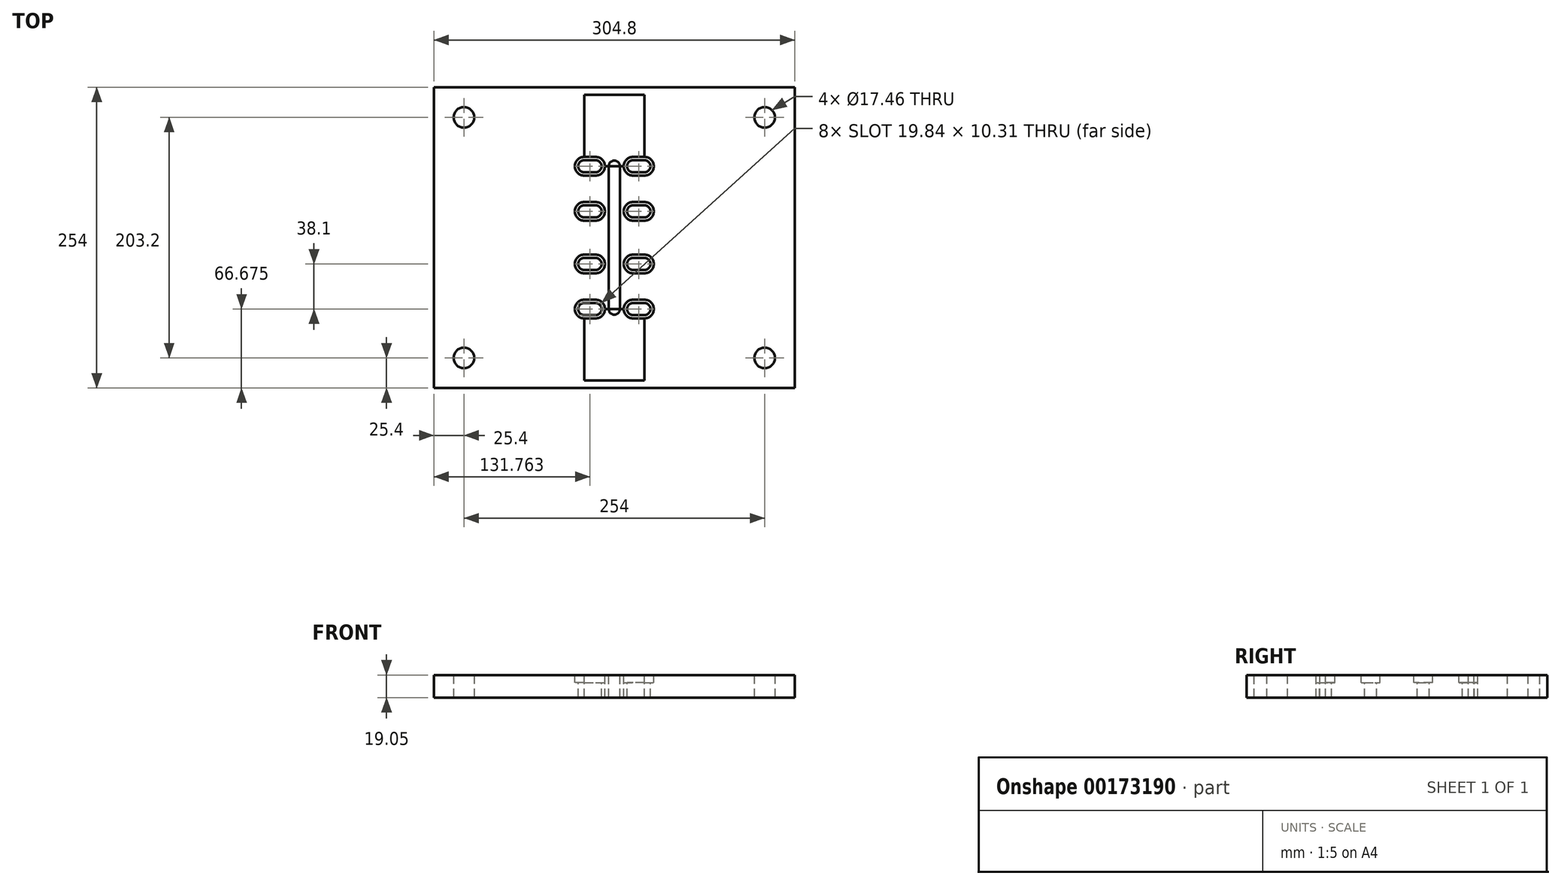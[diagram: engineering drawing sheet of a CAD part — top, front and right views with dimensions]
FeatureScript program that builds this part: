
annotation { "Feature Type Name" : "Feature", "Feature Type Description" : "" }
export const myFeature = defineFeature(function(context is Context, id is Id, definition is map)
    precondition{}
    {
        {
            var Q0;
            Q0=qCreatedBy(makeId("Top.planeOp"),FACE);
            var sketch = newSketch(context, id + "F0", { "sketchPlane" : qUnion([Q0])});
            skLineSegment(sketch, "E0.bottom", {"start": v(-152.4, 127) * mm, "end": v(152.4, 127) * mm});
            skLineSegment(sketch, "E0.top", {"start": v(-152.4, -127) * mm, "end": v(152.4, -127) * mm});
            skLineSegment(sketch, "E0.left", {"start": v(-152.4, 127) * mm, "end": v(-152.4, -127) * mm});
            skLineSegment(sketch, "E0.right", {"start": v(152.4, 127) * mm, "end": v(152.4, -127) * mm});
            skPoint(sketch, "E0.middle", {"position": v(0, 0) * mm});
            skLineSegment(sketch, "E1", {"start": v(0, 127) * mm, "end": v(0, -127) * mm});
            skLineSegment(sketch, "E2", {"start": v(152.4, 0) * mm, "end": v(-152.4, 0) * mm});
            skLineSegment(sketch, "E3.0", {"start": v(-22.22, 101.6) * mm, "end": v(-22.23, -101.6) * mm});
            skLineSegment(sketch, "E4.0", {"start": v(22.23, 101.6) * mm, "end": v(22.22, -101.6) * mm});
            skLineSegment(sketch, "E5.0", {"start": v(101.6, -22.22) * mm, "end": v(-101.6, -22.23) * mm});
            skLineSegment(sketch, "E6.0", {"start": v(101.6, 22.23) * mm, "end": v(-101.6, 22.22) * mm});
            skLineSegment(sketch, "E7.0", {"start": v(101.6, 60.33) * mm, "end": v(-101.6, 60.32) * mm});
            skLineSegment(sketch, "E8.0", {"start": v(101.6, -60.32) * mm, "end": v(-101.6, -60.33) * mm});
            skPoint(sketch, "E9", {"position": v(-22.22, 60.33) * mm});
            skPoint(sketch, "E10", {"position": v(22.23, 60.33) * mm});
            skPoint(sketch, "E11", {"position": v(22.23, 22.23) * mm});
            skPoint(sketch, "E12", {"position": v(-22.22, 22.23) * mm});
            skPoint(sketch, "E13", {"position": v(-22.23, -22.23) * mm});
            skPoint(sketch, "E14", {"position": v(22.22, -60.33) * mm});
            skPoint(sketch, "E15", {"position": v(22.22, -22.22) * mm});
            skPoint(sketch, "E16", {"position": v(-22.23, -60.33) * mm});
            skSolve(sketch);
        }
        {
            var Q0;
            Q0 = qSketchRegion(id + "F0", true);
            var Q1;
            {var subQ0=sQuery(id+"F0.wireOp",EDGE,"E7.0");var subQ1=sQuery(id+"F0.wireOp",EDGE,"E1");var subQ2=makeQuery(id+"F0.imprint","INTERSECT",VERTEX,{"derivedFrom":[subQ1,subQ0]});Q1=makeQuery(id+"F0.imprint","IMPRINT",FACE,{"disambiguationData":[TD([[makeQuery(id+"F0.imprint","IMPRINT",EDGE,{"disambiguationData":[TD([[subQ2,-1.0]])],"derivedFrom":subQ1}),-1.0]])]});}
            var Q2;
            {var subQ0=sQuery(id+"F0.wireOp",EDGE,"E7.0");var subQ1=sQuery(id+"F0.wireOp",EDGE,"E1");var subQ2=makeQuery(id+"F0.imprint","INTERSECT",VERTEX,{"derivedFrom":[subQ1,subQ0]});Q2=makeQuery(id+"F0.imprint","IMPRINT",FACE,{"disambiguationData":[TD([[makeQuery(id+"F0.imprint","IMPRINT",EDGE,{"disambiguationData":[TD([[subQ2,-1.0]])],"derivedFrom":subQ1}),1.0]])]});}
            var Q3;
            {var subQ0=sQuery(id+"F0.wireOp",EDGE,"E6.0");var subQ1=sQuery(id+"F0.wireOp",EDGE,"E1");var subQ2=makeQuery(id+"F0.imprint","INTERSECT",VERTEX,{"derivedFrom":[subQ1,subQ0]});Q3=makeQuery(id+"F0.imprint","IMPRINT",FACE,{"disambiguationData":[TD([[makeQuery(id+"F0.imprint","IMPRINT",EDGE,{"disambiguationData":[TD([[subQ2,-1.0]])],"derivedFrom":subQ1}),1.0]])]});}
            var Q4;
            {var subQ0=sQuery(id+"F0.wireOp",EDGE,"E6.0");var subQ1=sQuery(id+"F0.wireOp",EDGE,"E1");var subQ2=makeQuery(id+"F0.imprint","INTERSECT",VERTEX,{"derivedFrom":[subQ1,subQ0]});Q4=makeQuery(id+"F0.imprint","IMPRINT",FACE,{"disambiguationData":[TD([[makeQuery(id+"F0.imprint","IMPRINT",EDGE,{"disambiguationData":[TD([[subQ2,-1.0]])],"derivedFrom":subQ1}),-1.0]])]});}
            var Q5;
            {var subQ0=sQuery(id+"F0.wireOp",EDGE,"E2");var subQ1=sQuery(id+"F0.wireOp",EDGE,"E1");var subQ2=makeQuery(id+"F0.imprint","INTERSECT",VERTEX,{"derivedFrom":[subQ1,subQ0]});Q5=makeQuery(id+"F0.imprint","IMPRINT",FACE,{"disambiguationData":[TD([[makeQuery(id+"F0.imprint","IMPRINT",EDGE,{"disambiguationData":[TD([[subQ2,-1.0]])],"derivedFrom":subQ1}),-1.0]])]});}
            var Q6;
            {var subQ0=sQuery(id+"F0.wireOp",EDGE,"E2");var subQ1=sQuery(id+"F0.wireOp",EDGE,"E1");var subQ2=makeQuery(id+"F0.imprint","INTERSECT",VERTEX,{"derivedFrom":[subQ1,subQ0]});Q6=makeQuery(id+"F0.imprint","IMPRINT",FACE,{"disambiguationData":[TD([[makeQuery(id+"F0.imprint","IMPRINT",EDGE,{"disambiguationData":[TD([[subQ2,-1.0]])],"derivedFrom":subQ1}),1.0]])]});}
            var Q7;
            {var subQ0=sQuery(id+"F0.wireOp",EDGE,"E5.0");var subQ1=sQuery(id+"F0.wireOp",EDGE,"E1");var subQ2=makeQuery(id+"F0.imprint","INTERSECT",VERTEX,{"derivedFrom":[subQ1,subQ0]});Q7=makeQuery(id+"F0.imprint","IMPRINT",FACE,{"disambiguationData":[TD([[makeQuery(id+"F0.imprint","IMPRINT",EDGE,{"disambiguationData":[TD([[subQ2,-1.0]])],"derivedFrom":subQ1}),1.0]])]});}
            var Q8;
            {var subQ0=sQuery(id+"F0.wireOp",EDGE,"E5.0");var subQ1=sQuery(id+"F0.wireOp",EDGE,"E1");var subQ2=makeQuery(id+"F0.imprint","INTERSECT",VERTEX,{"derivedFrom":[subQ1,subQ0]});Q8=makeQuery(id+"F0.imprint","IMPRINT",FACE,{"disambiguationData":[TD([[makeQuery(id+"F0.imprint","IMPRINT",EDGE,{"disambiguationData":[TD([[subQ2,-1.0]])],"derivedFrom":subQ1}),-1.0]])]});}
            extrude(context, id + "F1", {"entities" : qUnion([Q0, Q1, Q2, Q3, Q4, Q5, Q6, Q7, Q8]), "depth" : 19.05 * mm});
        }
        {
            var Q0;
            Q0=makeQuery(id+"F1.opExtrude","CAP_FACE",FACE,{"disambiguationData":[OSD([sQuery(id+"F0.wireOp",EDGE,"E0.bottom"),sQuery(id+"F0.wireOp",EDGE,"E0.top"),sQuery(id+"F0.wireOp",EDGE,"E0.left"),sQuery(id+"F0.wireOp",EDGE,"E0.right")])],"isStart":false});
            var sketch = newSketch(context, id + "F2", { "sketchPlane" : qUnion([Q0])});
            skLineSegment(sketch, "E17", {"start": v(0, 127) * mm, "end": v(0, 120.65) * mm});
            skLineSegment(sketch, "E18", {"start": v(25.4, 127) * mm, "end": v(25.4, -127) * mm});
            skLineSegment(sketch, "E19", {"start": v(-25.4, -127) * mm, "end": v(-25.4, 127) * mm});
            skLineSegment(sketch, "E20", {"start": v(-152.4, 0) * mm, "end": v(152.4, 0) * mm});
            skLineSegment(sketch, "E21", {"start": v(152.4, 22.22) * mm, "end": v(-10.72, 22.22) * mm});
            skLineSegment(sketch, "E22", {"start": v(-152.4, 60.32) * mm, "end": v(152.4, 60.32) * mm});
            skLineSegment(sketch, "E23", {"start": v(152.4, -22.22) * mm, "end": v(-152.4, -22.23) * mm});
            skLineSegment(sketch, "E24", {"start": v(-152.4, -60.33) * mm, "end": v(152.4, -60.32) * mm});
            skLineSegment(sketch, "E25.0", {"start": v(-15.87, -101.6) * mm, "end": v(-15.88, 101.6) * mm});
            skLineSegment(sketch, "E26.0", {"start": v(15.87, 101.6) * mm, "end": v(15.88, -101.6) * mm});
            skLineSegment(sketch, "E27.0", {"start": v(146.05, -120.65) * mm, "end": v(146.05, 120.65) * mm});
            skLineSegment(sketch, "E27.1", {"start": v(-146.05, -120.65) * mm, "end": v(146.05, -120.65) * mm});
            skLineSegment(sketch, "E27.2", {"start": v(-146.05, 120.65) * mm, "end": v(-146.05, -120.65) * mm});
            skLineSegment(sketch, "E27.3", {"start": v(146.05, 120.65) * mm, "end": v(-146.05, 120.65) * mm});
            skArc(sketch, "E28", {"start": v(-25.4, 27.38) * mm, "mid": v(-30.56, 22.22) * mm, "end": v(-25.4, 17.07) * mm});
            skArc(sketch, "E29", {"start": v(-15.88, 17.07) * mm, "mid": v(-10.72, 22.22) * mm, "end": v(-15.88, 27.38) * mm});
            skLineSegment(sketch, "E30", {"start": v(-25.4, 27.38) * mm, "end": v(-15.88, 27.38) * mm});
            skLineSegment(sketch, "E31", {"start": v(-25.4, 17.07) * mm, "end": v(-15.88, 17.07) * mm});
            skLineSegment(sketch, "E32", {"start": v(-152.4, 41.27) * mm, "end": v(152.4, 41.28) * mm});
            skLineSegment(sketch, "E33", {"start": v(-152.4, -41.28) * mm, "end": v(152.4, -41.27) * mm});
            skLineSegment(sketch, "E34.trimOffspring", {"start": v(-146.05, 22.23) * mm, "end": v(-152.4, 22.23) * mm});
            skLineSegment(sketch, "E35.trimOffspring", {"start": v(-15.88, 22.22) * mm, "end": v(-25.4, 22.22) * mm});
            skArc(sketch, "E36.0.startCap", {"start": v(-15.88, 30.16) * mm, "mid": v(-7.94, 22.22) * mm, "end": v(-15.88, 14.29) * mm});
            skArc(sketch, "E36.0.endCap", {"start": v(-25.4, 14.29) * mm, "mid": v(-33.34, 22.22) * mm, "end": v(-25.4, 30.16) * mm});
            skLineSegment(sketch, "E36.0.left", {"start": v(-15.88, 14.29) * mm, "end": v(-25.4, 14.29) * mm});
            skLineSegment(sketch, "E36.0.right", {"start": v(-15.88, 30.16) * mm, "end": v(-25.4, 30.16) * mm});
            skLineSegment(sketch, "E37.MirrorCS", {"start": v(-15.88, 52.39) * mm, "end": v(-25.4, 52.39) * mm});
            skArc(sketch, "E38.MirrorCS", {"start": v(-15.88, 52.39) * mm, "mid": v(-7.94, 60.33) * mm, "end": v(-15.88, 68.26) * mm});
            skLineSegment(sketch, "E39.MirrorCS", {"start": v(-15.88, 68.26) * mm, "end": v(-25.4, 68.26) * mm});
            skArc(sketch, "E40.MirrorCS", {"start": v(-25.4, 68.26) * mm, "mid": v(-33.34, 60.32) * mm, "end": v(-25.4, 52.39) * mm});
            skArc(sketch, "E41.MirrorCS", {"start": v(-25.4, 55.17) * mm, "mid": v(-30.56, 60.32) * mm, "end": v(-25.4, 65.48) * mm});
            skLineSegment(sketch, "E42.MirrorCS", {"start": v(-25.4, 55.17) * mm, "end": v(-15.88, 55.17) * mm});
            skArc(sketch, "E43.MirrorCS", {"start": v(-15.88, 65.48) * mm, "mid": v(-10.72, 60.33) * mm, "end": v(-15.88, 55.17) * mm});
            skLineSegment(sketch, "E44.MirrorCS", {"start": v(-25.4, 65.48) * mm, "end": v(-15.88, 65.48) * mm});
            skLineSegment(sketch, "E45.MirrorCS", {"start": v(15.88, 68.26) * mm, "end": v(25.4, 68.26) * mm});
            skArc(sketch, "E46.MirrorCS", {"start": v(15.88, 52.39) * mm, "mid": v(7.94, 60.33) * mm, "end": v(15.88, 68.26) * mm});
            skLineSegment(sketch, "E47.MirrorCS", {"start": v(15.88, 52.39) * mm, "end": v(25.4, 52.39) * mm});
            skArc(sketch, "E48.MirrorCS", {"start": v(25.4, 68.26) * mm, "mid": v(33.34, 60.32) * mm, "end": v(25.4, 52.39) * mm});
            skArc(sketch, "E49.MirrorCS", {"start": v(25.4, 55.17) * mm, "mid": v(30.56, 60.32) * mm, "end": v(25.4, 65.48) * mm});
            skLineSegment(sketch, "E50.MirrorCS", {"start": v(25.4, 65.48) * mm, "end": v(15.88, 65.48) * mm});
            skArc(sketch, "E51.MirrorCS", {"start": v(15.88, 65.48) * mm, "mid": v(10.72, 60.33) * mm, "end": v(15.88, 55.17) * mm});
            skLineSegment(sketch, "E52.MirrorCS", {"start": v(25.4, 55.17) * mm, "end": v(15.88, 55.17) * mm});
            skLineSegment(sketch, "E53.MirrorCS", {"start": v(15.88, 30.16) * mm, "end": v(25.4, 30.16) * mm});
            skArc(sketch, "E54.MirrorCS", {"start": v(15.88, 30.16) * mm, "mid": v(7.94, 22.22) * mm, "end": v(15.87, 14.29) * mm});
            skLineSegment(sketch, "E55.MirrorCS", {"start": v(15.87, 14.29) * mm, "end": v(25.4, 14.29) * mm});
            skArc(sketch, "E56.MirrorCS", {"start": v(25.4, 14.29) * mm, "mid": v(33.34, 22.22) * mm, "end": v(25.4, 30.16) * mm});
            skArc(sketch, "E57.MirrorCS", {"start": v(25.4, 27.38) * mm, "mid": v(30.56, 22.22) * mm, "end": v(25.4, 17.07) * mm});
            skLineSegment(sketch, "E58.MirrorCS", {"start": v(25.4, 27.38) * mm, "end": v(15.88, 27.38) * mm});
            skArc(sketch, "E59.MirrorCS", {"start": v(15.88, 17.07) * mm, "mid": v(10.72, 22.22) * mm, "end": v(15.88, 27.38) * mm});
            skLineSegment(sketch, "E60.MirrorCS", {"start": v(25.4, 17.07) * mm, "end": v(15.87, 17.07) * mm});
            skLineSegment(sketch, "E61.MirrorCS", {"start": v(-15.88, -14.29) * mm, "end": v(-25.4, -14.29) * mm});
            skArc(sketch, "E62.MirrorCS", {"start": v(-25.4, -14.29) * mm, "mid": v(-33.34, -22.23) * mm, "end": v(-25.4, -30.16) * mm});
            skLineSegment(sketch, "E63.MirrorCS", {"start": v(-15.88, -30.16) * mm, "end": v(-25.4, -30.16) * mm});
            skArc(sketch, "E64.MirrorCS", {"start": v(-15.88, -30.16) * mm, "mid": v(-7.94, -22.23) * mm, "end": v(-15.88, -14.29) * mm});
            skArc(sketch, "E65.MirrorCS", {"start": v(-15.88, -17.07) * mm, "mid": v(-10.72, -22.23) * mm, "end": v(-15.88, -27.38) * mm});
            skLineSegment(sketch, "E66.MirrorCS", {"start": v(-25.4, -27.38) * mm, "end": v(-15.88, -27.38) * mm});
            skArc(sketch, "E67.MirrorCS", {"start": v(-25.4, -27.38) * mm, "mid": v(-30.56, -22.23) * mm, "end": v(-25.4, -17.07) * mm});
            skLineSegment(sketch, "E68.MirrorCS", {"start": v(-25.4, -17.07) * mm, "end": v(-15.88, -17.07) * mm});
            skLineSegment(sketch, "E69.MirrorCS", {"start": v(-15.88, -52.39) * mm, "end": v(-25.4, -52.39) * mm});
            skArc(sketch, "E70.MirrorCS", {"start": v(-25.4, -68.26) * mm, "mid": v(-33.34, -60.33) * mm, "end": v(-25.4, -52.39) * mm});
            skArc(sketch, "E71.MirrorCS", {"start": v(-15.88, -52.39) * mm, "mid": v(-7.94, -60.33) * mm, "end": v(-15.88, -68.26) * mm});
            skLineSegment(sketch, "E72.MirrorCS", {"start": v(-15.88, -68.26) * mm, "end": v(-25.4, -68.26) * mm});
            skLineSegment(sketch, "E73.MirrorCS", {"start": v(-25.4, -65.48) * mm, "end": v(-15.88, -65.48) * mm});
            skArc(sketch, "E74.MirrorCS", {"start": v(-25.4, -55.17) * mm, "mid": v(-30.56, -60.33) * mm, "end": v(-25.4, -65.48) * mm});
            skArc(sketch, "E75.MirrorCS", {"start": v(-15.88, -65.48) * mm, "mid": v(-10.72, -60.33) * mm, "end": v(-15.88, -55.17) * mm});
            skLineSegment(sketch, "E76.MirrorCS", {"start": v(-25.4, -55.17) * mm, "end": v(-15.88, -55.17) * mm});
            skLineSegment(sketch, "E77.MirrorCS", {"start": v(15.88, -68.26) * mm, "end": v(25.4, -68.26) * mm});
            skArc(sketch, "E78.MirrorCS", {"start": v(25.4, -68.26) * mm, "mid": v(33.34, -60.32) * mm, "end": v(25.4, -52.39) * mm});
            skLineSegment(sketch, "E79.MirrorCS", {"start": v(15.88, -52.39) * mm, "end": v(25.4, -52.39) * mm});
            skArc(sketch, "E80.MirrorCS", {"start": v(15.88, -52.39) * mm, "mid": v(7.94, -60.33) * mm, "end": v(15.88, -68.26) * mm});
            skArc(sketch, "E81.MirrorCS", {"start": v(15.88, -65.48) * mm, "mid": v(10.72, -60.33) * mm, "end": v(15.88, -55.17) * mm});
            skLineSegment(sketch, "E82.MirrorCS", {"start": v(25.4, -65.48) * mm, "end": v(15.88, -65.48) * mm});
            skArc(sketch, "E83.MirrorCS", {"start": v(25.4, -55.17) * mm, "mid": v(30.56, -60.33) * mm, "end": v(25.4, -65.48) * mm});
            skLineSegment(sketch, "E84.MirrorCS", {"start": v(25.4, -55.17) * mm, "end": v(15.88, -55.17) * mm});
            skLineSegment(sketch, "E85.MirrorCS", {"start": v(15.88, -30.16) * mm, "end": v(25.4, -30.16) * mm});
            skArc(sketch, "E86.MirrorCS", {"start": v(25.4, -14.29) * mm, "mid": v(33.34, -22.23) * mm, "end": v(25.4, -30.16) * mm});
            skArc(sketch, "E87.MirrorCS", {"start": v(25.4, -27.38) * mm, "mid": v(30.56, -22.23) * mm, "end": v(25.4, -17.07) * mm});
            skLineSegment(sketch, "E88.MirrorCS", {"start": v(25.4, -27.38) * mm, "end": v(15.88, -27.38) * mm});
            skLineSegment(sketch, "E89.MirrorCS", {"start": v(25.4, -17.07) * mm, "end": v(15.87, -17.07) * mm});
            skArc(sketch, "E90.MirrorCS", {"start": v(15.88, -17.07) * mm, "mid": v(10.72, -22.23) * mm, "end": v(15.88, -27.38) * mm});
            skArc(sketch, "E91.MirrorCS", {"start": v(15.88, -30.16) * mm, "mid": v(7.94, -22.23) * mm, "end": v(15.87, -14.29) * mm});
            skLineSegment(sketch, "E92.MirrorCS", {"start": v(15.87, -14.29) * mm, "end": v(25.4, -14.29) * mm});
            skLineSegment(sketch, "E93.trimOffspring", {"start": v(0, 60.32) * mm, "end": v(0, -60.33) * mm});
            skLineSegment(sketch, "E94.trimOffspring", {"start": v(0, -120.65) * mm, "end": v(0, -127) * mm});
            skArc(sketch, "E95.0.startCap", {"start": v(-4.76, 60.32) * mm, "mid": v(0, 65.09) * mm, "end": v(4.76, 60.32) * mm});
            skArc(sketch, "E95.0.endCap", {"start": v(4.76, -60.33) * mm, "mid": v(0, -65.09) * mm, "end": v(-4.76, -60.33) * mm});
            skLineSegment(sketch, "E95.0.left", {"start": v(4.76, 60.32) * mm, "end": v(4.76, -60.33) * mm});
            skLineSegment(sketch, "E95.0.right", {"start": v(-4.76, 60.32) * mm, "end": v(-4.76, -60.33) * mm});
            skSolve(sketch);
        }
        {
            var Q0;
            {var subQ3=sQuery(id+"F2.wireOp",EDGE,"E35.trimOffspring");var subQ5=sQuery(id+"F2.wireOp",EDGE,"E25.0");var subQ6=makeQuery(id+"F2.imprint","INTERSECT",VERTEX,{"derivedFrom":[subQ5,subQ3]});Q0=makeQuery(id+"F2.imprint","IMPRINT",FACE,{"disambiguationData":[TD([[makeQuery(id+"F2.imprint","IMPRINT",EDGE,{"disambiguationData":[TD([[subQ6,-1.0]])],"derivedFrom":subQ5}),1.0]])]});}
            var Q1;
            {var subQ0=sQuery(id+"F2.wireOp",EDGE,"E28");Q1=makeQuery(id+"F2.imprint","IMPRINT",FACE,{"disambiguationData":[TD([[makeQuery(id+"F2.imprint","IMPRINT",EDGE,{"derivedFrom":subQ0}),1.0]])]});}
            var Q2;
            {var subQ3=sQuery(id+"F2.wireOp",EDGE,"E35.trimOffspring");var subQ5=sQuery(id+"F2.wireOp",EDGE,"E25.0");var subQ6=makeQuery(id+"F2.imprint","INTERSECT",VERTEX,{"derivedFrom":[subQ5,subQ3]});Q2=makeQuery(id+"F2.imprint","IMPRINT",FACE,{"disambiguationData":[TD([[makeQuery(id+"F2.imprint","IMPRINT",EDGE,{"disambiguationData":[TD([[subQ6,1.0]])],"derivedFrom":subQ5}),1.0]])]});}
            var Q3;
            {var subQ6=sQuery(id+"F2.wireOp",EDGE,"E25.0");var subQ7=makeQuery(id+"F2.imprint","INTERSECT",VERTEX,{"derivedFrom":[subQ6,sQuery(id+"F2.wireOp",EDGE,"E35.trimOffspring")]});Q3=makeQuery(id+"F2.imprint","IMPRINT",FACE,{"disambiguationData":[TD([[makeQuery(id+"F2.imprint","IMPRINT",EDGE,{"disambiguationData":[TD([[subQ7,1.0]])],"derivedFrom":subQ6}),-1.0]])]});}
            var Q4;
            {var subQ0=sQuery(id+"F2.wireOp",EDGE,"E44.MirrorCS");Q4=makeQuery(id+"F2.imprint","IMPRINT",FACE,{"disambiguationData":[TD([[makeQuery(id+"F2.imprint","IMPRINT",EDGE,{"derivedFrom":subQ0}),-1.0]])]});}
            var Q5;
            {var subQ1=sQuery(id+"F2.wireOp",EDGE,"E19");var subQ3=sQuery(id+"F2.wireOp",EDGE,"E22");var subQ4=makeQuery(id+"F2.imprint","INTERSECT",VERTEX,{"derivedFrom":[subQ1,subQ3]});Q5=makeQuery(id+"F2.imprint","IMPRINT",FACE,{"disambiguationData":[TD([[makeQuery(id+"F2.imprint","IMPRINT",EDGE,{"disambiguationData":[TD([[subQ4,1.0]])],"derivedFrom":subQ3}),1.0]])]});}
            var Q6;
            {var subQ1=sQuery(id+"F2.wireOp",EDGE,"E19");var subQ3=sQuery(id+"F2.wireOp",EDGE,"E22");var subQ4=makeQuery(id+"F2.imprint","INTERSECT",VERTEX,{"derivedFrom":[subQ1,subQ3]});Q6=makeQuery(id+"F2.imprint","IMPRINT",FACE,{"disambiguationData":[TD([[makeQuery(id+"F2.imprint","IMPRINT",EDGE,{"disambiguationData":[TD([[subQ4,1.0]])],"derivedFrom":subQ3}),-1.0]])]});}
            var Q7;
            {var subQ0=sQuery(id+"F2.wireOp",EDGE,"E42.MirrorCS");Q7=makeQuery(id+"F2.imprint","IMPRINT",FACE,{"disambiguationData":[TD([[makeQuery(id+"F2.imprint","IMPRINT",EDGE,{"derivedFrom":subQ0}),1.0]])]});}
            var Q8;
            {var subQ0=sQuery(id+"F2.wireOp",EDGE,"E25.0");var subQ1=sQuery(id+"F2.wireOp",EDGE,"E22");var subQ2=makeQuery(id+"F2.imprint","INTERSECT",VERTEX,{"derivedFrom":[subQ1,subQ0]});Q8=makeQuery(id+"F2.imprint","IMPRINT",FACE,{"disambiguationData":[TD([[makeQuery(id+"F2.imprint","IMPRINT",EDGE,{"disambiguationData":[TD([[subQ2,-1.0]])],"derivedFrom":subQ1}),-1.0]])]});}
            var Q9;
            {var subQ0=sQuery(id+"F2.wireOp",EDGE,"E25.0");var subQ1=sQuery(id+"F2.wireOp",EDGE,"E22");var subQ2=makeQuery(id+"F2.imprint","INTERSECT",VERTEX,{"derivedFrom":[subQ1,subQ0]});Q9=makeQuery(id+"F2.imprint","IMPRINT",FACE,{"disambiguationData":[TD([[makeQuery(id+"F2.imprint","IMPRINT",EDGE,{"disambiguationData":[TD([[subQ2,-1.0]])],"derivedFrom":subQ1}),1.0]])]});}
            var Q10;
            {var subQ0=sQuery(id+"F2.wireOp",EDGE,"E51.MirrorCS");var subQ1=sQuery(id+"F2.wireOp",EDGE,"E22");var subQ2=makeQuery(id+"F2.imprint","INTERSECT",VERTEX,{"derivedFrom":[subQ1,subQ0]});Q10=makeQuery(id+"F2.imprint","IMPRINT",FACE,{"disambiguationData":[TD([[makeQuery(id+"F2.imprint","IMPRINT",EDGE,{"disambiguationData":[TD([[subQ2,-1.0]])],"derivedFrom":subQ1}),1.0]])]});}
            var Q11;
            {var subQ0=sQuery(id+"F2.wireOp",EDGE,"E50.MirrorCS");Q11=makeQuery(id+"F2.imprint","IMPRINT",FACE,{"disambiguationData":[TD([[makeQuery(id+"F2.imprint","IMPRINT",EDGE,{"derivedFrom":subQ0}),1.0]])]});}
            var Q12;
            {var subQ1=sQuery(id+"F2.wireOp",EDGE,"E18");var subQ3=sQuery(id+"F2.wireOp",EDGE,"E22");var subQ4=makeQuery(id+"F2.imprint","INTERSECT",VERTEX,{"derivedFrom":[subQ1,subQ3]});Q12=makeQuery(id+"F2.imprint","IMPRINT",FACE,{"disambiguationData":[TD([[makeQuery(id+"F2.imprint","IMPRINT",EDGE,{"disambiguationData":[TD([[subQ4,-1.0]])],"derivedFrom":subQ3}),1.0]])]});}
            var Q13;
            {var subQ1=sQuery(id+"F2.wireOp",EDGE,"E18");var subQ3=sQuery(id+"F2.wireOp",EDGE,"E22");var subQ4=makeQuery(id+"F2.imprint","INTERSECT",VERTEX,{"derivedFrom":[subQ1,subQ3]});Q13=makeQuery(id+"F2.imprint","IMPRINT",FACE,{"disambiguationData":[TD([[makeQuery(id+"F2.imprint","IMPRINT",EDGE,{"disambiguationData":[TD([[subQ4,-1.0]])],"derivedFrom":subQ3}),-1.0]])]});}
            var Q14;
            {var subQ0=sQuery(id+"F2.wireOp",EDGE,"E52.MirrorCS");Q14=makeQuery(id+"F2.imprint","IMPRINT",FACE,{"disambiguationData":[TD([[makeQuery(id+"F2.imprint","IMPRINT",EDGE,{"derivedFrom":subQ0}),-1.0]])]});}
            var Q15;
            {var subQ0=sQuery(id+"F2.wireOp",EDGE,"E51.MirrorCS");var subQ1=sQuery(id+"F2.wireOp",EDGE,"E22");var subQ2=makeQuery(id+"F2.imprint","INTERSECT",VERTEX,{"derivedFrom":[subQ1,subQ0]});Q15=makeQuery(id+"F2.imprint","IMPRINT",FACE,{"disambiguationData":[TD([[makeQuery(id+"F2.imprint","IMPRINT",EDGE,{"disambiguationData":[TD([[subQ2,-1.0]])],"derivedFrom":subQ1}),-1.0]])]});}
            var Q16;
            {var subQ0=sQuery(id+"F2.wireOp",EDGE,"E93.trimOffspring");var subQ5=sQuery(id+"F2.wireOp",EDGE,"E32");var subQ6=makeQuery(id+"F2.imprint","INTERSECT",VERTEX,{"derivedFrom":[subQ5,subQ0]});Q16=makeQuery(id+"F2.imprint","IMPRINT",FACE,{"disambiguationData":[TD([[makeQuery(id+"F2.imprint","IMPRINT",EDGE,{"disambiguationData":[TD([[subQ6,-1.0]])],"derivedFrom":subQ5}),1.0]])]});}
            var Q17;
            {var subQ3=sQuery(id+"F2.wireOp",EDGE,"E95.0.right");var subQ5=sQuery(id+"F2.wireOp",EDGE,"E32");var subQ6=makeQuery(id+"F2.imprint","INTERSECT",VERTEX,{"derivedFrom":[subQ5,subQ3]});Q17=makeQuery(id+"F2.imprint","IMPRINT",FACE,{"disambiguationData":[TD([[makeQuery(id+"F2.imprint","IMPRINT",EDGE,{"disambiguationData":[TD([[subQ6,-1.0]])],"derivedFrom":subQ5}),1.0]])]});}
            var Q18;
            {var subQ2=sQuery(id+"F2.wireOp",EDGE,"E95.0.startCap");Q18=makeQuery(id+"F2.imprint","IMPRINT",FACE,{"disambiguationData":[TD([[makeQuery(id+"F2.imprint","IMPRINT",EDGE,{"derivedFrom":subQ2}),-1.0]])]});}
            var Q19;
            {var subQ0=sQuery(id+"F2.wireOp",EDGE,"E93.trimOffspring");var subQ1=sQuery(id+"F2.wireOp",EDGE,"E21");var subQ2=makeQuery(id+"F2.imprint","INTERSECT",VERTEX,{"derivedFrom":[subQ1,subQ0]});Q19=makeQuery(id+"F2.imprint","IMPRINT",FACE,{"disambiguationData":[TD([[makeQuery(id+"F2.imprint","IMPRINT",EDGE,{"disambiguationData":[TD([[subQ2,-1.0]])],"derivedFrom":subQ1}),-1.0]])]});}
            var Q20;
            {var subQ0=sQuery(id+"F2.wireOp",EDGE,"E95.0.left");var subQ1=sQuery(id+"F2.wireOp",EDGE,"E21");var subQ2=makeQuery(id+"F2.imprint","INTERSECT",VERTEX,{"derivedFrom":[subQ1,subQ0]});Q20=makeQuery(id+"F2.imprint","IMPRINT",FACE,{"disambiguationData":[TD([[makeQuery(id+"F2.imprint","IMPRINT",EDGE,{"disambiguationData":[TD([[subQ2,-1.0]])],"derivedFrom":subQ1}),-1.0]])]});}
            var Q21;
            {var subQ0=sQuery(id+"F2.wireOp",EDGE,"E93.trimOffspring");var subQ1=sQuery(id+"F2.wireOp",EDGE,"E20");var subQ2=makeQuery(id+"F2.imprint","INTERSECT",VERTEX,{"derivedFrom":[subQ1,subQ0]});Q21=makeQuery(id+"F2.imprint","IMPRINT",FACE,{"disambiguationData":[TD([[makeQuery(id+"F2.imprint","IMPRINT",EDGE,{"disambiguationData":[TD([[subQ2,-1.0]])],"derivedFrom":subQ1}),-1.0]])]});}
            var Q22;
            {var subQ0=sQuery(id+"F2.wireOp",EDGE,"E95.0.right");var subQ1=sQuery(id+"F2.wireOp",EDGE,"E20");var subQ2=makeQuery(id+"F2.imprint","INTERSECT",VERTEX,{"derivedFrom":[subQ1,subQ0]});Q22=makeQuery(id+"F2.imprint","IMPRINT",FACE,{"disambiguationData":[TD([[makeQuery(id+"F2.imprint","IMPRINT",EDGE,{"disambiguationData":[TD([[subQ2,-1.0]])],"derivedFrom":subQ1}),-1.0]])]});}
            var Q23;
            {var subQ0=sQuery(id+"F2.wireOp",EDGE,"E95.0.left");var subQ1=sQuery(id+"F2.wireOp",EDGE,"E23");var subQ2=makeQuery(id+"F2.imprint","INTERSECT",VERTEX,{"derivedFrom":[subQ1,subQ0]});Q23=makeQuery(id+"F2.imprint","IMPRINT",FACE,{"disambiguationData":[TD([[makeQuery(id+"F2.imprint","IMPRINT",EDGE,{"disambiguationData":[TD([[subQ2,-1.0]])],"derivedFrom":subQ1}),1.0]])]});}
            var Q24;
            {var subQ0=sQuery(id+"F2.wireOp",EDGE,"E93.trimOffspring");var subQ1=sQuery(id+"F2.wireOp",EDGE,"E23");var subQ2=makeQuery(id+"F2.imprint","INTERSECT",VERTEX,{"derivedFrom":[subQ1,subQ0]});Q24=makeQuery(id+"F2.imprint","IMPRINT",FACE,{"disambiguationData":[TD([[makeQuery(id+"F2.imprint","IMPRINT",EDGE,{"disambiguationData":[TD([[subQ2,-1.0]])],"derivedFrom":subQ1}),1.0]])]});}
            var Q25;
            {var subQ3=sQuery(id+"F2.wireOp",EDGE,"E95.0.right");var subQ5=sQuery(id+"F2.wireOp",EDGE,"E33");var subQ6=makeQuery(id+"F2.imprint","INTERSECT",VERTEX,{"derivedFrom":[subQ5,subQ3]});Q25=makeQuery(id+"F2.imprint","IMPRINT",FACE,{"disambiguationData":[TD([[makeQuery(id+"F2.imprint","IMPRINT",EDGE,{"disambiguationData":[TD([[subQ6,-1.0]])],"derivedFrom":subQ5}),-1.0]])]});}
            var Q26;
            {var subQ2=sQuery(id+"F2.wireOp",EDGE,"E95.0.endCap");Q26=makeQuery(id+"F2.imprint","IMPRINT",FACE,{"disambiguationData":[TD([[makeQuery(id+"F2.imprint","IMPRINT",EDGE,{"derivedFrom":subQ2}),-1.0]])]});}
            var Q27;
            {var subQ0=sQuery(id+"F2.wireOp",EDGE,"E93.trimOffspring");var subQ1=sQuery(id+"F2.wireOp",EDGE,"E20");var subQ2=makeQuery(id+"F2.imprint","INTERSECT",VERTEX,{"derivedFrom":[subQ1,subQ0]});Q27=makeQuery(id+"F2.imprint","IMPRINT",FACE,{"disambiguationData":[TD([[makeQuery(id+"F2.imprint","IMPRINT",EDGE,{"disambiguationData":[TD([[subQ2,-1.0]])],"derivedFrom":subQ1}),1.0]])]});}
            var Q28;
            {var subQ0=sQuery(id+"F2.wireOp",EDGE,"E95.0.right");var subQ1=sQuery(id+"F2.wireOp",EDGE,"E20");var subQ2=makeQuery(id+"F2.imprint","INTERSECT",VERTEX,{"derivedFrom":[subQ1,subQ0]});Q28=makeQuery(id+"F2.imprint","IMPRINT",FACE,{"disambiguationData":[TD([[makeQuery(id+"F2.imprint","IMPRINT",EDGE,{"disambiguationData":[TD([[subQ2,-1.0]])],"derivedFrom":subQ1}),1.0]])]});}
            var Q29;
            {var subQ0=sQuery(id+"F2.wireOp",EDGE,"E26.0");var subQ1=sQuery(id+"F2.wireOp",EDGE,"E21");var subQ2=makeQuery(id+"F2.imprint","INTERSECT",VERTEX,{"derivedFrom":[subQ1,subQ0]});Q29=makeQuery(id+"F2.imprint","IMPRINT",FACE,{"disambiguationData":[TD([[makeQuery(id+"F2.imprint","IMPRINT",EDGE,{"disambiguationData":[TD([[subQ2,-1.0]])],"derivedFrom":subQ1}),1.0]])]});}
            var Q30;
            {var subQ0=sQuery(id+"F2.wireOp",EDGE,"E26.0");var subQ1=sQuery(id+"F2.wireOp",EDGE,"E21");var subQ2=makeQuery(id+"F2.imprint","INTERSECT",VERTEX,{"derivedFrom":[subQ1,subQ0]});Q30=makeQuery(id+"F2.imprint","IMPRINT",FACE,{"disambiguationData":[TD([[makeQuery(id+"F2.imprint","IMPRINT",EDGE,{"disambiguationData":[TD([[subQ2,-1.0]])],"derivedFrom":subQ1}),-1.0]])]});}
            var Q31;
            {var subQ1=sQuery(id+"F2.wireOp",EDGE,"E18");var subQ3=sQuery(id+"F2.wireOp",EDGE,"E21");var subQ4=makeQuery(id+"F2.imprint","INTERSECT",VERTEX,{"derivedFrom":[subQ1,subQ3]});Q31=makeQuery(id+"F2.imprint","IMPRINT",FACE,{"disambiguationData":[TD([[makeQuery(id+"F2.imprint","IMPRINT",EDGE,{"disambiguationData":[TD([[subQ4,1.0]])],"derivedFrom":subQ3}),-1.0]])]});}
            var Q32;
            {var subQ1=sQuery(id+"F2.wireOp",EDGE,"E18");var subQ3=sQuery(id+"F2.wireOp",EDGE,"E21");var subQ4=makeQuery(id+"F2.imprint","INTERSECT",VERTEX,{"derivedFrom":[subQ1,subQ3]});Q32=makeQuery(id+"F2.imprint","IMPRINT",FACE,{"disambiguationData":[TD([[makeQuery(id+"F2.imprint","IMPRINT",EDGE,{"disambiguationData":[TD([[subQ4,1.0]])],"derivedFrom":subQ3}),1.0]])]});}
            var Q33;
            {var subQ0=sQuery(id+"F2.wireOp",EDGE,"E60.MirrorCS");Q33=makeQuery(id+"F2.imprint","IMPRINT",FACE,{"disambiguationData":[TD([[makeQuery(id+"F2.imprint","IMPRINT",EDGE,{"derivedFrom":subQ0}),-1.0]])]});}
            var Q34;
            {var subQ0=sQuery(id+"F2.wireOp",EDGE,"E58.MirrorCS");Q34=makeQuery(id+"F2.imprint","IMPRINT",FACE,{"disambiguationData":[TD([[makeQuery(id+"F2.imprint","IMPRINT",EDGE,{"derivedFrom":subQ0}),1.0]])]});}
            var Q35;
            {var subQ0=sQuery(id+"F2.wireOp",EDGE,"E89.MirrorCS");Q35=makeQuery(id+"F2.imprint","IMPRINT",FACE,{"disambiguationData":[TD([[makeQuery(id+"F2.imprint","IMPRINT",EDGE,{"derivedFrom":subQ0}),1.0]])]});}
            var Q36;
            {var subQ0=sQuery(id+"F2.wireOp",EDGE,"E26.0");var subQ1=sQuery(id+"F2.wireOp",EDGE,"E23");var subQ2=makeQuery(id+"F2.imprint","INTERSECT",VERTEX,{"derivedFrom":[subQ1,subQ0]});Q36=makeQuery(id+"F2.imprint","IMPRINT",FACE,{"disambiguationData":[TD([[makeQuery(id+"F2.imprint","IMPRINT",EDGE,{"disambiguationData":[TD([[subQ2,-1.0]])],"derivedFrom":subQ1}),-1.0]])]});}
            var Q37;
            {var subQ0=sQuery(id+"F2.wireOp",EDGE,"E26.0");var subQ1=sQuery(id+"F2.wireOp",EDGE,"E23");var subQ2=makeQuery(id+"F2.imprint","INTERSECT",VERTEX,{"derivedFrom":[subQ1,subQ0]});Q37=makeQuery(id+"F2.imprint","IMPRINT",FACE,{"disambiguationData":[TD([[makeQuery(id+"F2.imprint","IMPRINT",EDGE,{"disambiguationData":[TD([[subQ2,-1.0]])],"derivedFrom":subQ1}),1.0]])]});}
            var Q38;
            {var subQ0=sQuery(id+"F2.wireOp",EDGE,"E88.MirrorCS");Q38=makeQuery(id+"F2.imprint","IMPRINT",FACE,{"disambiguationData":[TD([[makeQuery(id+"F2.imprint","IMPRINT",EDGE,{"derivedFrom":subQ0}),-1.0]])]});}
            var Q39;
            {var subQ1=sQuery(id+"F2.wireOp",EDGE,"E18");var subQ3=sQuery(id+"F2.wireOp",EDGE,"E23");var subQ4=makeQuery(id+"F2.imprint","INTERSECT",VERTEX,{"derivedFrom":[subQ1,subQ3]});Q39=makeQuery(id+"F2.imprint","IMPRINT",FACE,{"disambiguationData":[TD([[makeQuery(id+"F2.imprint","IMPRINT",EDGE,{"disambiguationData":[TD([[subQ4,1.0]])],"derivedFrom":subQ3}),1.0]])]});}
            var Q40;
            {var subQ1=sQuery(id+"F2.wireOp",EDGE,"E18");var subQ3=sQuery(id+"F2.wireOp",EDGE,"E23");var subQ4=makeQuery(id+"F2.imprint","INTERSECT",VERTEX,{"derivedFrom":[subQ1,subQ3]});Q40=makeQuery(id+"F2.imprint","IMPRINT",FACE,{"disambiguationData":[TD([[makeQuery(id+"F2.imprint","IMPRINT",EDGE,{"disambiguationData":[TD([[subQ4,1.0]])],"derivedFrom":subQ3}),-1.0]])]});}
            var Q41;
            {var subQ0=sQuery(id+"F2.wireOp",EDGE,"E84.MirrorCS");Q41=makeQuery(id+"F2.imprint","IMPRINT",FACE,{"disambiguationData":[TD([[makeQuery(id+"F2.imprint","IMPRINT",EDGE,{"derivedFrom":subQ0}),1.0]])]});}
            var Q42;
            {var subQ0=sQuery(id+"F2.wireOp",EDGE,"E81.MirrorCS");var subQ1=sQuery(id+"F2.wireOp",EDGE,"E24");var subQ2=makeQuery(id+"F2.imprint","INTERSECT",VERTEX,{"derivedFrom":[subQ1,subQ0]});Q42=makeQuery(id+"F2.imprint","IMPRINT",FACE,{"disambiguationData":[TD([[makeQuery(id+"F2.imprint","IMPRINT",EDGE,{"disambiguationData":[TD([[subQ2,-1.0]])],"derivedFrom":subQ1}),1.0]])]});}
            var Q43;
            {var subQ0=sQuery(id+"F2.wireOp",EDGE,"E81.MirrorCS");var subQ1=sQuery(id+"F2.wireOp",EDGE,"E24");var subQ2=makeQuery(id+"F2.imprint","INTERSECT",VERTEX,{"derivedFrom":[subQ1,subQ0]});Q43=makeQuery(id+"F2.imprint","IMPRINT",FACE,{"disambiguationData":[TD([[makeQuery(id+"F2.imprint","IMPRINT",EDGE,{"disambiguationData":[TD([[subQ2,-1.0]])],"derivedFrom":subQ1}),-1.0]])]});}
            var Q44;
            {var subQ0=sQuery(id+"F2.wireOp",EDGE,"E82.MirrorCS");Q44=makeQuery(id+"F2.imprint","IMPRINT",FACE,{"disambiguationData":[TD([[makeQuery(id+"F2.imprint","IMPRINT",EDGE,{"derivedFrom":subQ0}),-1.0]])]});}
            var Q45;
            {var subQ1=sQuery(id+"F2.wireOp",EDGE,"E18");var subQ3=sQuery(id+"F2.wireOp",EDGE,"E24");var subQ4=makeQuery(id+"F2.imprint","INTERSECT",VERTEX,{"derivedFrom":[subQ1,subQ3]});Q45=makeQuery(id+"F2.imprint","IMPRINT",FACE,{"disambiguationData":[TD([[makeQuery(id+"F2.imprint","IMPRINT",EDGE,{"disambiguationData":[TD([[subQ4,-1.0]])],"derivedFrom":subQ3}),1.0]])]});}
            var Q46;
            {var subQ1=sQuery(id+"F2.wireOp",EDGE,"E18");var subQ3=sQuery(id+"F2.wireOp",EDGE,"E24");var subQ4=makeQuery(id+"F2.imprint","INTERSECT",VERTEX,{"derivedFrom":[subQ1,subQ3]});Q46=makeQuery(id+"F2.imprint","IMPRINT",FACE,{"disambiguationData":[TD([[makeQuery(id+"F2.imprint","IMPRINT",EDGE,{"disambiguationData":[TD([[subQ4,-1.0]])],"derivedFrom":subQ3}),-1.0]])]});}
            var Q47;
            {var subQ0=sQuery(id+"F2.wireOp",EDGE,"E65.MirrorCS");var subQ1=sQuery(id+"F2.wireOp",EDGE,"E23");var subQ2=makeQuery(id+"F2.imprint","INTERSECT",VERTEX,{"derivedFrom":[subQ1,subQ0]});Q47=makeQuery(id+"F2.imprint","IMPRINT",FACE,{"disambiguationData":[TD([[makeQuery(id+"F2.imprint","IMPRINT",EDGE,{"disambiguationData":[TD([[subQ2,-1.0]])],"derivedFrom":subQ1}),-1.0]])]});}
            var Q48;
            {var subQ0=sQuery(id+"F2.wireOp",EDGE,"E68.MirrorCS");Q48=makeQuery(id+"F2.imprint","IMPRINT",FACE,{"disambiguationData":[TD([[makeQuery(id+"F2.imprint","IMPRINT",EDGE,{"derivedFrom":subQ0}),-1.0]])]});}
            var Q49;
            {var subQ1=sQuery(id+"F2.wireOp",EDGE,"E19");var subQ3=sQuery(id+"F2.wireOp",EDGE,"E23");var subQ4=makeQuery(id+"F2.imprint","INTERSECT",VERTEX,{"derivedFrom":[subQ1,subQ3]});Q49=makeQuery(id+"F2.imprint","IMPRINT",FACE,{"disambiguationData":[TD([[makeQuery(id+"F2.imprint","IMPRINT",EDGE,{"disambiguationData":[TD([[subQ4,-1.0]])],"derivedFrom":subQ3}),-1.0]])]});}
            var Q50;
            {var subQ1=sQuery(id+"F2.wireOp",EDGE,"E19");var subQ3=sQuery(id+"F2.wireOp",EDGE,"E23");var subQ4=makeQuery(id+"F2.imprint","INTERSECT",VERTEX,{"derivedFrom":[subQ1,subQ3]});Q50=makeQuery(id+"F2.imprint","IMPRINT",FACE,{"disambiguationData":[TD([[makeQuery(id+"F2.imprint","IMPRINT",EDGE,{"disambiguationData":[TD([[subQ4,-1.0]])],"derivedFrom":subQ3}),1.0]])]});}
            var Q51;
            {var subQ0=sQuery(id+"F2.wireOp",EDGE,"E66.MirrorCS");Q51=makeQuery(id+"F2.imprint","IMPRINT",FACE,{"disambiguationData":[TD([[makeQuery(id+"F2.imprint","IMPRINT",EDGE,{"derivedFrom":subQ0}),1.0]])]});}
            var Q52;
            {var subQ0=sQuery(id+"F2.wireOp",EDGE,"E65.MirrorCS");var subQ1=sQuery(id+"F2.wireOp",EDGE,"E23");var subQ2=makeQuery(id+"F2.imprint","INTERSECT",VERTEX,{"derivedFrom":[subQ1,subQ0]});Q52=makeQuery(id+"F2.imprint","IMPRINT",FACE,{"disambiguationData":[TD([[makeQuery(id+"F2.imprint","IMPRINT",EDGE,{"disambiguationData":[TD([[subQ2,-1.0]])],"derivedFrom":subQ1}),1.0]])]});}
            var Q53;
            {var subQ0=sQuery(id+"F2.wireOp",EDGE,"E25.0");var subQ1=sQuery(id+"F2.wireOp",EDGE,"E24");var subQ2=makeQuery(id+"F2.imprint","INTERSECT",VERTEX,{"derivedFrom":[subQ1,subQ0]});Q53=makeQuery(id+"F2.imprint","IMPRINT",FACE,{"disambiguationData":[TD([[makeQuery(id+"F2.imprint","IMPRINT",EDGE,{"disambiguationData":[TD([[subQ2,-1.0]])],"derivedFrom":subQ1}),1.0]])]});}
            var Q54;
            {var subQ0=sQuery(id+"F2.wireOp",EDGE,"E76.MirrorCS");Q54=makeQuery(id+"F2.imprint","IMPRINT",FACE,{"disambiguationData":[TD([[makeQuery(id+"F2.imprint","IMPRINT",EDGE,{"derivedFrom":subQ0}),-1.0]])]});}
            var Q55;
            {var subQ1=sQuery(id+"F2.wireOp",EDGE,"E19");var subQ3=sQuery(id+"F2.wireOp",EDGE,"E24");var subQ4=makeQuery(id+"F2.imprint","INTERSECT",VERTEX,{"derivedFrom":[subQ1,subQ3]});Q55=makeQuery(id+"F2.imprint","IMPRINT",FACE,{"disambiguationData":[TD([[makeQuery(id+"F2.imprint","IMPRINT",EDGE,{"disambiguationData":[TD([[subQ4,1.0]])],"derivedFrom":subQ3}),1.0]])]});}
            var Q56;
            {var subQ1=sQuery(id+"F2.wireOp",EDGE,"E19");var subQ3=sQuery(id+"F2.wireOp",EDGE,"E24");var subQ4=makeQuery(id+"F2.imprint","INTERSECT",VERTEX,{"derivedFrom":[subQ1,subQ3]});Q56=makeQuery(id+"F2.imprint","IMPRINT",FACE,{"disambiguationData":[TD([[makeQuery(id+"F2.imprint","IMPRINT",EDGE,{"disambiguationData":[TD([[subQ4,1.0]])],"derivedFrom":subQ3}),-1.0]])]});}
            var Q57;
            {var subQ0=sQuery(id+"F2.wireOp",EDGE,"E73.MirrorCS");Q57=makeQuery(id+"F2.imprint","IMPRINT",FACE,{"disambiguationData":[TD([[makeQuery(id+"F2.imprint","IMPRINT",EDGE,{"derivedFrom":subQ0}),1.0]])]});}
            var Q58;
            {var subQ0=sQuery(id+"F2.wireOp",EDGE,"E25.0");var subQ1=sQuery(id+"F2.wireOp",EDGE,"E24");var subQ2=makeQuery(id+"F2.imprint","INTERSECT",VERTEX,{"derivedFrom":[subQ1,subQ0]});Q58=makeQuery(id+"F2.imprint","IMPRINT",FACE,{"disambiguationData":[TD([[makeQuery(id+"F2.imprint","IMPRINT",EDGE,{"disambiguationData":[TD([[subQ2,-1.0]])],"derivedFrom":subQ1}),-1.0]])]});}
            var Q59;
            {var subQ0=sQuery(id+"F2.wireOp",EDGE,"E93.trimOffspring");var subQ5=sQuery(id+"F2.wireOp",EDGE,"E33");var subQ6=makeQuery(id+"F2.imprint","INTERSECT",VERTEX,{"derivedFrom":[subQ5,subQ0]});Q59=makeQuery(id+"F2.imprint","IMPRINT",FACE,{"disambiguationData":[TD([[makeQuery(id+"F2.imprint","IMPRINT",EDGE,{"disambiguationData":[TD([[subQ6,-1.0]])],"derivedFrom":subQ5}),-1.0]])]});}
            extrude(context, id + "F3", {"entities" : qUnion([Q0, Q1, Q2, Q3, Q4, Q5, Q6, Q7, Q8, Q9, Q10, Q11, Q12, Q13, Q14, Q15, Q16, Q17, Q18, Q19, Q20, Q21, Q22, Q23, Q24, Q25, Q26, Q27, Q28, Q29, Q30, Q31, Q32, Q33, Q34, Q35, Q36, Q37, Q38, Q39, Q40, Q41, Q42, Q43, Q44, Q45, Q46, Q47, Q48, Q49, Q50, Q51, Q52, Q53, Q54, Q55, Q56, Q57, Q58, Q59]), "operationType" : NewBodyOperationType.REMOVE, "oppositeDirection" : true, "depth" : 25.4 * mm});
        }
        {
            var Q0;
            {var subQ0=sQuery(id+"F2.wireOp",EDGE,"E28");Q0=makeQuery(id+"F2.imprint","IMPRINT",FACE,{"disambiguationData":[TD([[makeQuery(id+"F2.imprint","IMPRINT",EDGE,{"derivedFrom":subQ0}),-1.0]])]});}
            var Q1;
            {var subQ0=sQuery(id+"F2.wireOp",EDGE,"E30");var subQ5=sQuery(id+"F2.wireOp",EDGE,"E25.0");var subQ6=makeQuery(id+"F2.imprint","INTERSECT",VERTEX,{"derivedFrom":[subQ5,subQ0]});Q1=makeQuery(id+"F2.imprint","IMPRINT",FACE,{"disambiguationData":[TD([[makeQuery(id+"F2.imprint","IMPRINT",EDGE,{"disambiguationData":[TD([[subQ6,-1.0]])],"derivedFrom":subQ5}),1.0]])]});}
            var Q2;
            {var subQ1=sQuery(id+"F2.wireOp",EDGE,"E29");var subQ5=sQuery(id+"F2.wireOp",EDGE,"E21");var subQ6=makeQuery(id+"F2.imprint","INTERSECT",VERTEX,{"derivedFrom":[subQ5,subQ1]});Q2=makeQuery(id+"F2.imprint","IMPRINT",FACE,{"disambiguationData":[TD([[makeQuery(id+"F2.imprint","IMPRINT",EDGE,{"disambiguationData":[TD([[subQ6,1.0]])],"derivedFrom":subQ5}),-1.0]])]});}
            var Q3;
            {var subQ1=sQuery(id+"F2.wireOp",EDGE,"E29");var subQ9=sQuery(id+"F2.wireOp",EDGE,"E21");var subQ10=makeQuery(id+"F2.imprint","INTERSECT",VERTEX,{"derivedFrom":[subQ9,subQ1]});Q3=makeQuery(id+"F2.imprint","IMPRINT",FACE,{"disambiguationData":[TD([[makeQuery(id+"F2.imprint","IMPRINT",EDGE,{"disambiguationData":[TD([[subQ10,1.0]])],"derivedFrom":subQ9}),1.0]])]});}
            var Q4;
            {var subQ3=sQuery(id+"F2.wireOp",EDGE,"E36.0.left");var subQ5=sQuery(id+"F2.wireOp",EDGE,"E25.0");var subQ6=makeQuery(id+"F2.imprint","INTERSECT",VERTEX,{"derivedFrom":[subQ5,subQ3]});Q4=makeQuery(id+"F2.imprint","IMPRINT",FACE,{"disambiguationData":[TD([[makeQuery(id+"F2.imprint","IMPRINT",EDGE,{"disambiguationData":[TD([[subQ6,-1.0]])],"derivedFrom":subQ5}),1.0]])]});}
            var Q5;
            {var subQ0=sQuery(id+"F2.wireOp",EDGE,"E40.MirrorCS");var subQ5=sQuery(id+"F2.wireOp",EDGE,"E22");var subQ6=makeQuery(id+"F2.imprint","INTERSECT",VERTEX,{"derivedFrom":[subQ5,subQ0]});Q5=makeQuery(id+"F2.imprint","IMPRINT",FACE,{"disambiguationData":[TD([[makeQuery(id+"F2.imprint","IMPRINT",EDGE,{"disambiguationData":[TD([[subQ6,-1.0]])],"derivedFrom":subQ5}),1.0]])]});}
            var Q6;
            {var subQ0=sQuery(id+"F2.wireOp",EDGE,"E39.MirrorCS");Q6=makeQuery(id+"F2.imprint","IMPRINT",FACE,{"disambiguationData":[TD([[makeQuery(id+"F2.imprint","IMPRINT",EDGE,{"derivedFrom":subQ0}),1.0]])]});}
            var Q7;
            {var subQ0=sQuery(id+"F2.wireOp",EDGE,"E43.MirrorCS");var subQ1=sQuery(id+"F2.wireOp",EDGE,"E22");var subQ2=makeQuery(id+"F2.imprint","INTERSECT",VERTEX,{"derivedFrom":[subQ1,subQ0]});Q7=makeQuery(id+"F2.imprint","IMPRINT",FACE,{"disambiguationData":[TD([[makeQuery(id+"F2.imprint","IMPRINT",EDGE,{"disambiguationData":[TD([[subQ2,-1.0]])],"derivedFrom":subQ1}),1.0]])]});}
            var Q8;
            {var subQ0=sQuery(id+"F2.wireOp",EDGE,"E43.MirrorCS");var subQ1=sQuery(id+"F2.wireOp",EDGE,"E22");var subQ2=makeQuery(id+"F2.imprint","INTERSECT",VERTEX,{"derivedFrom":[subQ1,subQ0]});Q8=makeQuery(id+"F2.imprint","IMPRINT",FACE,{"disambiguationData":[TD([[makeQuery(id+"F2.imprint","IMPRINT",EDGE,{"disambiguationData":[TD([[subQ2,-1.0]])],"derivedFrom":subQ1}),-1.0]])]});}
            var Q9;
            {var subQ0=sQuery(id+"F2.wireOp",EDGE,"E37.MirrorCS");Q9=makeQuery(id+"F2.imprint","IMPRINT",FACE,{"disambiguationData":[TD([[makeQuery(id+"F2.imprint","IMPRINT",EDGE,{"derivedFrom":subQ0}),-1.0]])]});}
            var Q10;
            {var subQ0=sQuery(id+"F2.wireOp",EDGE,"E40.MirrorCS");var subQ5=sQuery(id+"F2.wireOp",EDGE,"E22");var subQ6=makeQuery(id+"F2.imprint","INTERSECT",VERTEX,{"derivedFrom":[subQ5,subQ0]});Q10=makeQuery(id+"F2.imprint","IMPRINT",FACE,{"disambiguationData":[TD([[makeQuery(id+"F2.imprint","IMPRINT",EDGE,{"disambiguationData":[TD([[subQ6,-1.0]])],"derivedFrom":subQ5}),-1.0]])]});}
            var Q11;
            {var subQ0=sQuery(id+"F2.wireOp",EDGE,"E46.MirrorCS");var subQ1=sQuery(id+"F2.wireOp",EDGE,"E22");var subQ2=makeQuery(id+"F2.imprint","INTERSECT",VERTEX,{"derivedFrom":[subQ1,subQ0]});Q11=makeQuery(id+"F2.imprint","IMPRINT",FACE,{"disambiguationData":[TD([[makeQuery(id+"F2.imprint","IMPRINT",EDGE,{"disambiguationData":[TD([[subQ2,-1.0]])],"derivedFrom":subQ1}),-1.0]])]});}
            var Q12;
            {var subQ0=sQuery(id+"F2.wireOp",EDGE,"E46.MirrorCS");var subQ1=sQuery(id+"F2.wireOp",EDGE,"E22");var subQ2=makeQuery(id+"F2.imprint","INTERSECT",VERTEX,{"derivedFrom":[subQ1,subQ0]});Q12=makeQuery(id+"F2.imprint","IMPRINT",FACE,{"disambiguationData":[TD([[makeQuery(id+"F2.imprint","IMPRINT",EDGE,{"disambiguationData":[TD([[subQ2,-1.0]])],"derivedFrom":subQ1}),1.0]])]});}
            var Q13;
            {var subQ0=sQuery(id+"F2.wireOp",EDGE,"E45.MirrorCS");Q13=makeQuery(id+"F2.imprint","IMPRINT",FACE,{"disambiguationData":[TD([[makeQuery(id+"F2.imprint","IMPRINT",EDGE,{"derivedFrom":subQ0}),-1.0]])]});}
            var Q14;
            {var subQ3=sQuery(id+"F2.wireOp",EDGE,"E49.MirrorCS");var subQ5=sQuery(id+"F2.wireOp",EDGE,"E22");var subQ6=makeQuery(id+"F2.imprint","INTERSECT",VERTEX,{"derivedFrom":[subQ5,subQ3]});Q14=makeQuery(id+"F2.imprint","IMPRINT",FACE,{"disambiguationData":[TD([[makeQuery(id+"F2.imprint","IMPRINT",EDGE,{"disambiguationData":[TD([[subQ6,-1.0]])],"derivedFrom":subQ5}),1.0]])]});}
            var Q15;
            {var subQ3=sQuery(id+"F2.wireOp",EDGE,"E49.MirrorCS");var subQ5=sQuery(id+"F2.wireOp",EDGE,"E22");var subQ6=makeQuery(id+"F2.imprint","INTERSECT",VERTEX,{"derivedFrom":[subQ5,subQ3]});Q15=makeQuery(id+"F2.imprint","IMPRINT",FACE,{"disambiguationData":[TD([[makeQuery(id+"F2.imprint","IMPRINT",EDGE,{"disambiguationData":[TD([[subQ6,-1.0]])],"derivedFrom":subQ5}),-1.0]])]});}
            var Q16;
            {var subQ0=sQuery(id+"F2.wireOp",EDGE,"E47.MirrorCS");Q16=makeQuery(id+"F2.imprint","IMPRINT",FACE,{"disambiguationData":[TD([[makeQuery(id+"F2.imprint","IMPRINT",EDGE,{"derivedFrom":subQ0}),1.0]])]});}
            var Q17;
            {var subQ0=sQuery(id+"F2.wireOp",EDGE,"E53.MirrorCS");Q17=makeQuery(id+"F2.imprint","IMPRINT",FACE,{"disambiguationData":[TD([[makeQuery(id+"F2.imprint","IMPRINT",EDGE,{"derivedFrom":subQ0}),-1.0]])]});}
            var Q18;
            {var subQ0=sQuery(id+"F2.wireOp",EDGE,"E59.MirrorCS");var subQ1=sQuery(id+"F2.wireOp",EDGE,"E21");var subQ2=makeQuery(id+"F2.imprint","INTERSECT",VERTEX,{"derivedFrom":[subQ1,subQ0]});Q18=makeQuery(id+"F2.imprint","IMPRINT",FACE,{"disambiguationData":[TD([[makeQuery(id+"F2.imprint","IMPRINT",EDGE,{"disambiguationData":[TD([[subQ2,-1.0]])],"derivedFrom":subQ1}),1.0]])]});}
            var Q19;
            {var subQ0=sQuery(id+"F2.wireOp",EDGE,"E55.MirrorCS");Q19=makeQuery(id+"F2.imprint","IMPRINT",FACE,{"disambiguationData":[TD([[makeQuery(id+"F2.imprint","IMPRINT",EDGE,{"derivedFrom":subQ0}),1.0]])]});}
            var Q20;
            {var subQ0=sQuery(id+"F2.wireOp",EDGE,"E56.MirrorCS");var subQ5=sQuery(id+"F2.wireOp",EDGE,"E21");var subQ7=makeQuery(id+"F2.imprint","INTERSECT",VERTEX,{"derivedFrom":[subQ5,subQ0]});Q20=makeQuery(id+"F2.imprint","IMPRINT",FACE,{"disambiguationData":[TD([[makeQuery(id+"F2.imprint","IMPRINT",EDGE,{"disambiguationData":[TD([[subQ7,-1.0]])],"derivedFrom":subQ5}),1.0]])]});}
            var Q21;
            {var subQ0=sQuery(id+"F2.wireOp",EDGE,"E56.MirrorCS");var subQ5=sQuery(id+"F2.wireOp",EDGE,"E21");var subQ6=makeQuery(id+"F2.imprint","INTERSECT",VERTEX,{"derivedFrom":[subQ5,subQ0]});Q21=makeQuery(id+"F2.imprint","IMPRINT",FACE,{"disambiguationData":[TD([[makeQuery(id+"F2.imprint","IMPRINT",EDGE,{"disambiguationData":[TD([[subQ6,-1.0]])],"derivedFrom":subQ5}),-1.0]])]});}
            var Q22;
            {var subQ0=sQuery(id+"F2.wireOp",EDGE,"E59.MirrorCS");var subQ1=sQuery(id+"F2.wireOp",EDGE,"E21");var subQ2=makeQuery(id+"F2.imprint","INTERSECT",VERTEX,{"derivedFrom":[subQ1,subQ0]});Q22=makeQuery(id+"F2.imprint","IMPRINT",FACE,{"disambiguationData":[TD([[makeQuery(id+"F2.imprint","IMPRINT",EDGE,{"disambiguationData":[TD([[subQ2,-1.0]])],"derivedFrom":subQ1}),-1.0]])]});}
            var Q23;
            {var subQ0=sQuery(id+"F2.wireOp",EDGE,"E86.MirrorCS");var subQ5=sQuery(id+"F2.wireOp",EDGE,"E23");var subQ6=makeQuery(id+"F2.imprint","INTERSECT",VERTEX,{"derivedFrom":[subQ5,subQ0]});Q23=makeQuery(id+"F2.imprint","IMPRINT",FACE,{"disambiguationData":[TD([[makeQuery(id+"F2.imprint","IMPRINT",EDGE,{"disambiguationData":[TD([[subQ6,-1.0]])],"derivedFrom":subQ5}),-1.0]])]});}
            var Q24;
            {var subQ2=sQuery(id+"F2.wireOp",EDGE,"E89.MirrorCS");Q24=makeQuery(id+"F2.imprint","IMPRINT",FACE,{"disambiguationData":[TD([[makeQuery(id+"F2.imprint","IMPRINT",EDGE,{"derivedFrom":subQ2}),-1.0]])]});}
            var Q25;
            {var subQ0=sQuery(id+"F2.wireOp",EDGE,"E90.MirrorCS");var subQ1=sQuery(id+"F2.wireOp",EDGE,"E23");var subQ2=makeQuery(id+"F2.imprint","INTERSECT",VERTEX,{"derivedFrom":[subQ1,subQ0]});Q25=makeQuery(id+"F2.imprint","IMPRINT",FACE,{"disambiguationData":[TD([[makeQuery(id+"F2.imprint","IMPRINT",EDGE,{"disambiguationData":[TD([[subQ2,-1.0]])],"derivedFrom":subQ1}),-1.0]])]});}
            var Q26;
            {var subQ0=sQuery(id+"F2.wireOp",EDGE,"E90.MirrorCS");var subQ1=sQuery(id+"F2.wireOp",EDGE,"E23");var subQ2=makeQuery(id+"F2.imprint","INTERSECT",VERTEX,{"derivedFrom":[subQ1,subQ0]});Q26=makeQuery(id+"F2.imprint","IMPRINT",FACE,{"disambiguationData":[TD([[makeQuery(id+"F2.imprint","IMPRINT",EDGE,{"disambiguationData":[TD([[subQ2,-1.0]])],"derivedFrom":subQ1}),1.0]])]});}
            var Q27;
            {var subQ2=sQuery(id+"F2.wireOp",EDGE,"E88.MirrorCS");Q27=makeQuery(id+"F2.imprint","IMPRINT",FACE,{"disambiguationData":[TD([[makeQuery(id+"F2.imprint","IMPRINT",EDGE,{"derivedFrom":subQ2}),1.0]])]});}
            var Q28;
            {var subQ0=sQuery(id+"F2.wireOp",EDGE,"E86.MirrorCS");var subQ5=sQuery(id+"F2.wireOp",EDGE,"E23");var subQ6=makeQuery(id+"F2.imprint","INTERSECT",VERTEX,{"derivedFrom":[subQ5,subQ0]});Q28=makeQuery(id+"F2.imprint","IMPRINT",FACE,{"disambiguationData":[TD([[makeQuery(id+"F2.imprint","IMPRINT",EDGE,{"disambiguationData":[TD([[subQ6,-1.0]])],"derivedFrom":subQ5}),1.0]])]});}
            var Q29;
            {var subQ3=sQuery(id+"F2.wireOp",EDGE,"E83.MirrorCS");var subQ5=sQuery(id+"F2.wireOp",EDGE,"E24");var subQ6=makeQuery(id+"F2.imprint","INTERSECT",VERTEX,{"derivedFrom":[subQ5,subQ3]});Q29=makeQuery(id+"F2.imprint","IMPRINT",FACE,{"disambiguationData":[TD([[makeQuery(id+"F2.imprint","IMPRINT",EDGE,{"disambiguationData":[TD([[subQ6,-1.0]])],"derivedFrom":subQ5}),1.0]])]});}
            var Q30;
            {var subQ0=sQuery(id+"F2.wireOp",EDGE,"E79.MirrorCS");Q30=makeQuery(id+"F2.imprint","IMPRINT",FACE,{"disambiguationData":[TD([[makeQuery(id+"F2.imprint","IMPRINT",EDGE,{"derivedFrom":subQ0}),-1.0]])]});}
            var Q31;
            {var subQ0=sQuery(id+"F2.wireOp",EDGE,"E80.MirrorCS");var subQ1=sQuery(id+"F2.wireOp",EDGE,"E24");var subQ2=makeQuery(id+"F2.imprint","INTERSECT",VERTEX,{"derivedFrom":[subQ1,subQ0]});Q31=makeQuery(id+"F2.imprint","IMPRINT",FACE,{"disambiguationData":[TD([[makeQuery(id+"F2.imprint","IMPRINT",EDGE,{"disambiguationData":[TD([[subQ2,-1.0]])],"derivedFrom":subQ1}),1.0]])]});}
            var Q32;
            {var subQ0=sQuery(id+"F2.wireOp",EDGE,"E80.MirrorCS");var subQ1=sQuery(id+"F2.wireOp",EDGE,"E24");var subQ2=makeQuery(id+"F2.imprint","INTERSECT",VERTEX,{"derivedFrom":[subQ1,subQ0]});Q32=makeQuery(id+"F2.imprint","IMPRINT",FACE,{"disambiguationData":[TD([[makeQuery(id+"F2.imprint","IMPRINT",EDGE,{"disambiguationData":[TD([[subQ2,-1.0]])],"derivedFrom":subQ1}),-1.0]])]});}
            var Q33;
            {var subQ0=sQuery(id+"F2.wireOp",EDGE,"E77.MirrorCS");Q33=makeQuery(id+"F2.imprint","IMPRINT",FACE,{"disambiguationData":[TD([[makeQuery(id+"F2.imprint","IMPRINT",EDGE,{"derivedFrom":subQ0}),1.0]])]});}
            var Q34;
            {var subQ3=sQuery(id+"F2.wireOp",EDGE,"E83.MirrorCS");var subQ5=sQuery(id+"F2.wireOp",EDGE,"E24");var subQ6=makeQuery(id+"F2.imprint","INTERSECT",VERTEX,{"derivedFrom":[subQ5,subQ3]});Q34=makeQuery(id+"F2.imprint","IMPRINT",FACE,{"disambiguationData":[TD([[makeQuery(id+"F2.imprint","IMPRINT",EDGE,{"disambiguationData":[TD([[subQ6,-1.0]])],"derivedFrom":subQ5}),-1.0]])]});}
            var Q35;
            {var subQ0=sQuery(id+"F2.wireOp",EDGE,"E75.MirrorCS");var subQ1=sQuery(id+"F2.wireOp",EDGE,"E24");var subQ2=makeQuery(id+"F2.imprint","INTERSECT",VERTEX,{"derivedFrom":[subQ1,subQ0]});Q35=makeQuery(id+"F2.imprint","IMPRINT",FACE,{"disambiguationData":[TD([[makeQuery(id+"F2.imprint","IMPRINT",EDGE,{"disambiguationData":[TD([[subQ2,-1.0]])],"derivedFrom":subQ1}),-1.0]])]});}
            var Q36;
            {var subQ0=sQuery(id+"F2.wireOp",EDGE,"E75.MirrorCS");var subQ1=sQuery(id+"F2.wireOp",EDGE,"E24");var subQ2=makeQuery(id+"F2.imprint","INTERSECT",VERTEX,{"derivedFrom":[subQ1,subQ0]});Q36=makeQuery(id+"F2.imprint","IMPRINT",FACE,{"disambiguationData":[TD([[makeQuery(id+"F2.imprint","IMPRINT",EDGE,{"disambiguationData":[TD([[subQ2,-1.0]])],"derivedFrom":subQ1}),1.0]])]});}
            var Q37;
            {var subQ0=sQuery(id+"F2.wireOp",EDGE,"E69.MirrorCS");Q37=makeQuery(id+"F2.imprint","IMPRINT",FACE,{"disambiguationData":[TD([[makeQuery(id+"F2.imprint","IMPRINT",EDGE,{"derivedFrom":subQ0}),1.0]])]});}
            var Q38;
            {var subQ0=sQuery(id+"F2.wireOp",EDGE,"E70.MirrorCS");var subQ5=sQuery(id+"F2.wireOp",EDGE,"E24");var subQ6=makeQuery(id+"F2.imprint","INTERSECT",VERTEX,{"derivedFrom":[subQ5,subQ0]});Q38=makeQuery(id+"F2.imprint","IMPRINT",FACE,{"disambiguationData":[TD([[makeQuery(id+"F2.imprint","IMPRINT",EDGE,{"disambiguationData":[TD([[subQ6,-1.0]])],"derivedFrom":subQ5}),1.0]])]});}
            var Q39;
            {var subQ0=sQuery(id+"F2.wireOp",EDGE,"E70.MirrorCS");var subQ5=sQuery(id+"F2.wireOp",EDGE,"E24");var subQ6=makeQuery(id+"F2.imprint","INTERSECT",VERTEX,{"derivedFrom":[subQ5,subQ0]});Q39=makeQuery(id+"F2.imprint","IMPRINT",FACE,{"disambiguationData":[TD([[makeQuery(id+"F2.imprint","IMPRINT",EDGE,{"disambiguationData":[TD([[subQ6,-1.0]])],"derivedFrom":subQ5}),-1.0]])]});}
            var Q40;
            {var subQ0=sQuery(id+"F2.wireOp",EDGE,"E72.MirrorCS");Q40=makeQuery(id+"F2.imprint","IMPRINT",FACE,{"disambiguationData":[TD([[makeQuery(id+"F2.imprint","IMPRINT",EDGE,{"derivedFrom":subQ0}),-1.0]])]});}
            var Q41;
            {var subQ0=sQuery(id+"F2.wireOp",EDGE,"E61.MirrorCS");Q41=makeQuery(id+"F2.imprint","IMPRINT",FACE,{"disambiguationData":[TD([[makeQuery(id+"F2.imprint","IMPRINT",EDGE,{"derivedFrom":subQ0}),1.0]])]});}
            var Q42;
            {var subQ3=sQuery(id+"F2.wireOp",EDGE,"E67.MirrorCS");var subQ5=sQuery(id+"F2.wireOp",EDGE,"E23");var subQ6=makeQuery(id+"F2.imprint","INTERSECT",VERTEX,{"derivedFrom":[subQ5,subQ3]});Q42=makeQuery(id+"F2.imprint","IMPRINT",FACE,{"disambiguationData":[TD([[makeQuery(id+"F2.imprint","IMPRINT",EDGE,{"disambiguationData":[TD([[subQ6,-1.0]])],"derivedFrom":subQ5}),-1.0]])]});}
            var Q43;
            {var subQ3=sQuery(id+"F2.wireOp",EDGE,"E67.MirrorCS");var subQ5=sQuery(id+"F2.wireOp",EDGE,"E23");var subQ6=makeQuery(id+"F2.imprint","INTERSECT",VERTEX,{"derivedFrom":[subQ5,subQ3]});Q43=makeQuery(id+"F2.imprint","IMPRINT",FACE,{"disambiguationData":[TD([[makeQuery(id+"F2.imprint","IMPRINT",EDGE,{"disambiguationData":[TD([[subQ6,-1.0]])],"derivedFrom":subQ5}),1.0]])]});}
            var Q44;
            {var subQ0=sQuery(id+"F2.wireOp",EDGE,"E63.MirrorCS");Q44=makeQuery(id+"F2.imprint","IMPRINT",FACE,{"disambiguationData":[TD([[makeQuery(id+"F2.imprint","IMPRINT",EDGE,{"derivedFrom":subQ0}),-1.0]])]});}
            var Q45;
            {var subQ0=sQuery(id+"F2.wireOp",EDGE,"E64.MirrorCS");var subQ1=sQuery(id+"F2.wireOp",EDGE,"E23");var subQ2=makeQuery(id+"F2.imprint","INTERSECT",VERTEX,{"derivedFrom":[subQ1,subQ0]});Q45=makeQuery(id+"F2.imprint","IMPRINT",FACE,{"disambiguationData":[TD([[makeQuery(id+"F2.imprint","IMPRINT",EDGE,{"disambiguationData":[TD([[subQ2,-1.0]])],"derivedFrom":subQ1}),1.0]])]});}
            var Q46;
            {var subQ0=sQuery(id+"F2.wireOp",EDGE,"E64.MirrorCS");var subQ1=sQuery(id+"F2.wireOp",EDGE,"E23");var subQ2=makeQuery(id+"F2.imprint","INTERSECT",VERTEX,{"derivedFrom":[subQ1,subQ0]});Q46=makeQuery(id+"F2.imprint","IMPRINT",FACE,{"disambiguationData":[TD([[makeQuery(id+"F2.imprint","IMPRINT",EDGE,{"disambiguationData":[TD([[subQ2,-1.0]])],"derivedFrom":subQ1}),-1.0]])]});}
            extrude(context, id + "F4", {"entities" : qUnion([Q0, Q1, Q2, Q3, Q4, Q5, Q6, Q7, Q8, Q9, Q10, Q11, Q12, Q13, Q14, Q15, Q16, Q17, Q18, Q19, Q20, Q21, Q22, Q23, Q24, Q25, Q26, Q27, Q28, Q29, Q30, Q31, Q32, Q33, Q34, Q35, Q36, Q37, Q38, Q39, Q40, Q41, Q42, Q43, Q44, Q45, Q46]), "operationType" : NewBodyOperationType.REMOVE, "oppositeDirection" : true, "depth" : 6.35 * mm});
        }
        {
            var Q0;
            Q0=makeQuery(id+"F1.opExtrude","CAP_FACE",FACE,{"disambiguationData":[OSD([sQuery(id+"F0.wireOp",EDGE,"E0.bottom"),sQuery(id+"F0.wireOp",EDGE,"E0.top"),sQuery(id+"F0.wireOp",EDGE,"E0.left"),sQuery(id+"F0.wireOp",EDGE,"E0.right")])],"isStart":false});
            var sketch = newSketch(context, id + "F5", { "sketchPlane" : qUnion([Q0])});
            skPoint(sketch, "E96", {"position": v(-127, 101.6) * mm});
            skPoint(sketch, "E97.MirrorP", {"position": v(127, 101.6) * mm});
            skPoint(sketch, "E98.MirrorP", {"position": v(-127, -101.6) * mm});
            skPoint(sketch, "E99.MirrorP", {"position": v(127, -101.6) * mm});
            skSolve(sketch);
        }
        {
            var Q0;
            Q0=sQuery(id+"F5.wireOp",VERTEX,"E96");
            var Q1;
            Q1=sQuery(id+"F5.wireOp",VERTEX,"E97.MirrorP");
            var Q2;
            Q2=sQuery(id+"F5.wireOp",VERTEX,"E99.MirrorP");
            var Q3;
            Q3=sQuery(id+"F5.wireOp",VERTEX,"E98.MirrorP");
            var Q4;
            Q4=makeQuery(id+"F1.opExtrude","SWEPT_BODY",BODY,{"disambiguationData":[OSD([sQuery(id+"F0.wireOp",EDGE,"E0.bottom"),sQuery(id+"F0.wireOp",EDGE,"E0.top"),sQuery(id+"F0.wireOp",EDGE,"E0.left"),sQuery(id+"F0.wireOp",EDGE,"E0.right")])]});
            hole(context, id + "F6", {"style" : HoleStyle.SIMPLE, "endStyle" : HoleEndStyle.THROUGH, "holeDiameter" : 17.46 * mm, "tappedDepth" : 12.7 * mm, "tapClearance" : 3, "startFromSketch" : true, "locations" : qUnion([Q0, Q1, Q2, Q3]), "scope" : qUnion([Q4])});
        }
    });
